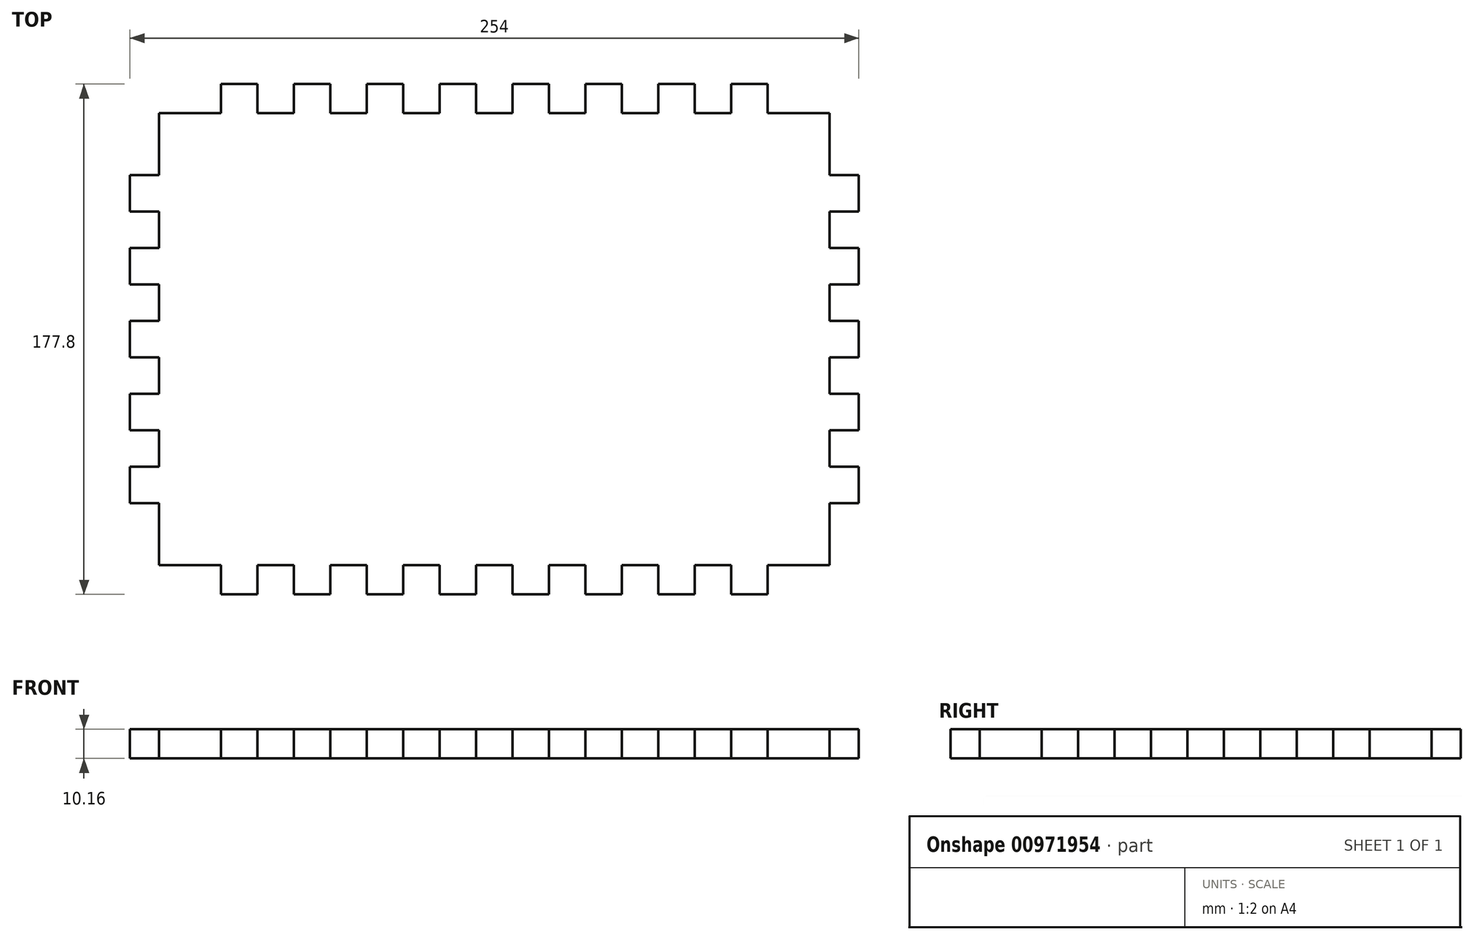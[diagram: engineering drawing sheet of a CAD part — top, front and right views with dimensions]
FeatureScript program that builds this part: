
annotation { "Feature Type Name" : "Feature", "Feature Type Description" : "" }
export const myFeature = defineFeature(function(context is Context, id is Id, definition is map)
    precondition{}
    {
        {
            var Q0;
            Q0=qCreatedBy(makeId("Top.planeOp"),FACE);
            var sketch = newSketch(context, id + "F0", { "sketchPlane" : qUnion([Q0])});
            skLineSegment(sketch, "E0.bottom", {"start": v(31.75, 0) * mm, "end": v(44.45, 0) * mm});
            skLineSegment(sketch, "E1", {"start": v(10.16, -10.16) * mm, "end": v(31.75, -10.16) * mm});
            skLineSegment(sketch, "E2", {"start": v(31.75, -10.16) * mm, "end": v(31.75, 0) * mm});
            skLineSegment(sketch, "E3", {"start": v(44.45, 0) * mm, "end": v(44.45, -10.16) * mm});
            skLineSegment(sketch, "E4", {"start": v(44.45, -10.16) * mm, "end": v(57.15, -10.16) * mm});
            skLineSegment(sketch, "E5", {"start": v(57.15, -10.16) * mm, "end": v(57.15, 0) * mm});
            skLineSegment(sketch, "E6", {"start": v(57.15, 0) * mm, "end": v(69.85, 0) * mm});
            skLineSegment(sketch, "E7", {"start": v(69.85, 0) * mm, "end": v(69.85, -10.16) * mm});
            skLineSegment(sketch, "E8", {"start": v(69.85, -10.16) * mm, "end": v(82.55, -10.16) * mm});
            skLineSegment(sketch, "E9", {"start": v(82.55, -10.16) * mm, "end": v(82.55, 0) * mm});
            skLineSegment(sketch, "E10", {"start": v(82.55, 0) * mm, "end": v(95.25, 0) * mm});
            skLineSegment(sketch, "E11", {"start": v(95.25, 0) * mm, "end": v(95.25, -10.16) * mm});
            skLineSegment(sketch, "E12", {"start": v(95.25, -10.16) * mm, "end": v(107.95, -10.16) * mm});
            skLineSegment(sketch, "E13", {"start": v(107.95, -10.16) * mm, "end": v(107.95, 0) * mm});
            skLineSegment(sketch, "E14", {"start": v(107.95, 0) * mm, "end": v(120.65, 0) * mm});
            skLineSegment(sketch, "E15", {"start": v(120.65, 0) * mm, "end": v(120.65, -10.16) * mm});
            skLineSegment(sketch, "E16", {"start": v(120.65, -10.16) * mm, "end": v(133.35, -10.16) * mm});
            skLineSegment(sketch, "E17", {"start": v(133.35, -10.16) * mm, "end": v(133.35, 0) * mm});
            skPoint(sketch, "E18.orphan", {"position": v(0, 0) * mm});
            skLineSegment(sketch, "E19.trimOffspring", {"start": v(133.35, 0) * mm, "end": v(146.05, 0) * mm});
            skLineSegment(sketch, "E20", {"start": v(146.05, 0) * mm, "end": v(146.05, -10.16) * mm});
            skLineSegment(sketch, "E21", {"start": v(146.05, -10.16) * mm, "end": v(158.75, -10.16) * mm});
            skLineSegment(sketch, "E22", {"start": v(158.75, -10.16) * mm, "end": v(158.75, 0) * mm});
            skLineSegment(sketch, "E23", {"start": v(158.75, 0) * mm, "end": v(171.45, 0) * mm});
            skLineSegment(sketch, "E24", {"start": v(171.45, 0) * mm, "end": v(171.45, -10.16) * mm});
            skLineSegment(sketch, "E25", {"start": v(171.45, -10.16) * mm, "end": v(184.15, -10.16) * mm});
            skLineSegment(sketch, "E26", {"start": v(184.15, -10.16) * mm, "end": v(184.15, 0) * mm});
            skLineSegment(sketch, "E27", {"start": v(184.15, 0) * mm, "end": v(196.85, 0) * mm});
            skLineSegment(sketch, "E28", {"start": v(196.85, 0) * mm, "end": v(196.85, -10.16) * mm});
            skLineSegment(sketch, "E29", {"start": v(196.85, -10.16) * mm, "end": v(209.55, -10.16) * mm});
            skLineSegment(sketch, "E30", {"start": v(209.55, -10.16) * mm, "end": v(209.55, 0) * mm});
            skLineSegment(sketch, "E31.trimOffspring", {"start": v(209.55, 0) * mm, "end": v(222.25, 0) * mm});
            skLineSegment(sketch, "E32", {"start": v(222.25, 0) * mm, "end": v(222.25, -10.16) * mm});
            skLineSegment(sketch, "E33", {"start": v(222.25, -10.16) * mm, "end": v(243.84, -10.16) * mm});
            skPoint(sketch, "E34.orphan", {"position": v(254, 0) * mm});
            skLineSegment(sketch, "E35", {"start": v(10.16, -167.64) * mm, "end": v(31.75, -167.64) * mm});
            skPoint(sketch, "E36.orphan", {"position": v(0, -177.8) * mm});
            skLineSegment(sketch, "E37", {"start": v(127, -10.16) * mm, "end": v(127, -10.16) * mm});
            skLineSegment(sketch, "E38.MirrorCS", {"start": v(222.25, -10.16) * mm, "end": v(222.25, 0) * mm});
            skLineSegment(sketch, "E39.MirrorCS", {"start": v(243.84, -10.16) * mm, "end": v(222.25, -10.16) * mm});
            skLineSegment(sketch, "E40.MirrorCS", {"start": v(243.84, -167.64) * mm, "end": v(222.25, -167.64) * mm});
            skLineSegment(sketch, "E41", {"start": v(10.16, -10.16) * mm, "end": v(10.16, -31.75) * mm});
            skLineSegment(sketch, "E42", {"start": v(10.16, -31.75) * mm, "end": v(0, -31.75) * mm});
            skLineSegment(sketch, "E43", {"start": v(0, -31.75) * mm, "end": v(0, -44.45) * mm});
            skLineSegment(sketch, "E44", {"start": v(0, -44.45) * mm, "end": v(10.16, -44.45) * mm});
            skLineSegment(sketch, "E45", {"start": v(10.16, -44.45) * mm, "end": v(10.16, -57.15) * mm});
            skLineSegment(sketch, "E46", {"start": v(10.16, -57.15) * mm, "end": v(0, -57.15) * mm});
            skLineSegment(sketch, "E47", {"start": v(0, -57.15) * mm, "end": v(0, -69.85) * mm});
            skLineSegment(sketch, "E48", {"start": v(0, -69.85) * mm, "end": v(10.16, -69.85) * mm});
            skLineSegment(sketch, "E49", {"start": v(10.16, -69.85) * mm, "end": v(10.16, -82.55) * mm});
            skLineSegment(sketch, "E50", {"start": v(10.16, -82.55) * mm, "end": v(0, -82.55) * mm});
            skLineSegment(sketch, "E51", {"start": v(0, -82.55) * mm, "end": v(0, -95.25) * mm});
            skLineSegment(sketch, "E52", {"start": v(0, -95.25) * mm, "end": v(10.16, -95.25) * mm});
            skLineSegment(sketch, "E53", {"start": v(10.16, -95.25) * mm, "end": v(10.16, -107.95) * mm});
            skLineSegment(sketch, "E54", {"start": v(10.16, -107.95) * mm, "end": v(0, -107.95) * mm});
            skLineSegment(sketch, "E55", {"start": v(0, -107.95) * mm, "end": v(0, -120.65) * mm});
            skLineSegment(sketch, "E56", {"start": v(0, -120.65) * mm, "end": v(10.16, -120.65) * mm});
            skLineSegment(sketch, "E57", {"start": v(10.16, -120.65) * mm, "end": v(10.16, -133.35) * mm});
            skLineSegment(sketch, "E58", {"start": v(10.16, -133.35) * mm, "end": v(0, -133.35) * mm});
            skLineSegment(sketch, "E59", {"start": v(0, -133.35) * mm, "end": v(0, -146.05) * mm});
            skLineSegment(sketch, "E60", {"start": v(0, -146.05) * mm, "end": v(10.16, -146.05) * mm});
            skLineSegment(sketch, "E61", {"start": v(10.16, -146.05) * mm, "end": v(10.16, -167.64) * mm});
            skLineSegment(sketch, "E62.MirrorCS", {"start": v(243.84, -10.16) * mm, "end": v(243.84, -31.75) * mm});
            skLineSegment(sketch, "E63.MirrorCS", {"start": v(254, -146.05) * mm, "end": v(243.84, -146.05) * mm});
            skLineSegment(sketch, "E64.MirrorCS", {"start": v(254, -44.45) * mm, "end": v(243.84, -44.45) * mm});
            skLineSegment(sketch, "E65.MirrorCS", {"start": v(243.84, -57.15) * mm, "end": v(254, -57.15) * mm});
            skLineSegment(sketch, "E66.MirrorCS", {"start": v(254, -120.65) * mm, "end": v(243.84, -120.65) * mm});
            skLineSegment(sketch, "E67.MirrorCS", {"start": v(243.84, -107.95) * mm, "end": v(254, -107.95) * mm});
            skLineSegment(sketch, "E68.MirrorCS", {"start": v(254, -69.85) * mm, "end": v(243.84, -69.85) * mm});
            skLineSegment(sketch, "E69.MirrorCS", {"start": v(243.84, -82.55) * mm, "end": v(254, -82.55) * mm});
            skLineSegment(sketch, "E70.MirrorCS", {"start": v(254, -95.25) * mm, "end": v(243.84, -95.25) * mm});
            skLineSegment(sketch, "E71.MirrorCS", {"start": v(243.84, -133.35) * mm, "end": v(254, -133.35) * mm});
            skLineSegment(sketch, "E72.MirrorCS", {"start": v(243.84, -31.75) * mm, "end": v(254, -31.75) * mm});
            skLineSegment(sketch, "E73.MirrorCS", {"start": v(254, -31.75) * mm, "end": v(254, -44.45) * mm});
            skLineSegment(sketch, "E74.MirrorCS", {"start": v(254, -107.95) * mm, "end": v(254, -120.65) * mm});
            skLineSegment(sketch, "E75.MirrorCS", {"start": v(254, -57.15) * mm, "end": v(254, -69.85) * mm});
            skLineSegment(sketch, "E76.MirrorCS", {"start": v(243.84, -69.85) * mm, "end": v(243.84, -82.55) * mm});
            skLineSegment(sketch, "E77.MirrorCS", {"start": v(254, -133.35) * mm, "end": v(254, -146.05) * mm});
            skLineSegment(sketch, "E78.MirrorCS", {"start": v(243.84, -95.25) * mm, "end": v(243.84, -107.95) * mm});
            skLineSegment(sketch, "E79.MirrorCS", {"start": v(243.84, -44.45) * mm, "end": v(243.84, -57.15) * mm});
            skLineSegment(sketch, "E80.MirrorCS", {"start": v(254, -82.55) * mm, "end": v(254, -95.25) * mm});
            skLineSegment(sketch, "E81.MirrorCS", {"start": v(243.84, -120.65) * mm, "end": v(243.84, -133.35) * mm});
            skLineSegment(sketch, "E82.MirrorCS", {"start": v(243.84, -146.05) * mm, "end": v(243.84, -167.64) * mm});
            skLineSegment(sketch, "E83", {"start": v(0, -88.9) * mm, "end": v(0, -88.9) * mm});
            skLineSegment(sketch, "E84.MirrorCS", {"start": v(222.25, -167.64) * mm, "end": v(222.25, -177.8) * mm});
            skLineSegment(sketch, "E85.MirrorCS", {"start": v(222.25, -177.8) * mm, "end": v(222.25, -167.64) * mm});
            skLineSegment(sketch, "E86.MirrorCS", {"start": v(31.75, -167.64) * mm, "end": v(31.75, -177.8) * mm});
            skLineSegment(sketch, "E87.MirrorCS", {"start": v(158.75, -167.64) * mm, "end": v(158.75, -177.8) * mm});
            skLineSegment(sketch, "E88.MirrorCS", {"start": v(146.05, -177.8) * mm, "end": v(146.05, -167.64) * mm});
            skLineSegment(sketch, "E89.MirrorCS", {"start": v(69.85, -177.8) * mm, "end": v(69.85, -167.64) * mm});
            skLineSegment(sketch, "E90.MirrorCS", {"start": v(95.25, -177.8) * mm, "end": v(95.25, -167.64) * mm});
            skLineSegment(sketch, "E91.MirrorCS", {"start": v(107.95, -167.64) * mm, "end": v(107.95, -177.8) * mm});
            skLineSegment(sketch, "E92.MirrorCS", {"start": v(120.65, -167.64) * mm, "end": v(133.35, -167.64) * mm});
            skLineSegment(sketch, "E93.MirrorCS", {"start": v(171.45, -177.8) * mm, "end": v(171.45, -167.64) * mm});
            skLineSegment(sketch, "E94.MirrorCS", {"start": v(196.85, -177.8) * mm, "end": v(196.85, -167.64) * mm});
            skLineSegment(sketch, "E95.MirrorCS", {"start": v(184.15, -167.64) * mm, "end": v(184.15, -177.8) * mm});
            skLineSegment(sketch, "E96.MirrorCS", {"start": v(57.15, -167.64) * mm, "end": v(57.15, -177.8) * mm});
            skLineSegment(sketch, "E97.MirrorCS", {"start": v(133.35, -167.64) * mm, "end": v(133.35, -177.8) * mm});
            skLineSegment(sketch, "E98.MirrorCS", {"start": v(44.45, -177.8) * mm, "end": v(44.45, -167.64) * mm});
            skLineSegment(sketch, "E99.MirrorCS", {"start": v(82.55, -167.64) * mm, "end": v(82.55, -177.8) * mm});
            skLineSegment(sketch, "E100.MirrorCS", {"start": v(209.55, -167.64) * mm, "end": v(209.55, -177.8) * mm});
            skLineSegment(sketch, "E101.MirrorCS", {"start": v(120.65, -177.8) * mm, "end": v(120.65, -167.64) * mm});
            skLineSegment(sketch, "E102.MirrorCS", {"start": v(184.15, -177.8) * mm, "end": v(196.85, -177.8) * mm});
            skLineSegment(sketch, "E103.MirrorCS", {"start": v(82.55, -177.8) * mm, "end": v(95.25, -177.8) * mm});
            skLineSegment(sketch, "E104.MirrorCS", {"start": v(209.55, -177.8) * mm, "end": v(222.25, -177.8) * mm});
            skLineSegment(sketch, "E105.MirrorCS", {"start": v(133.35, -177.8) * mm, "end": v(146.05, -177.8) * mm});
            skLineSegment(sketch, "E106.MirrorCS", {"start": v(57.15, -177.8) * mm, "end": v(69.85, -177.8) * mm});
            skLineSegment(sketch, "E107.MirrorCS", {"start": v(31.75, -177.8) * mm, "end": v(44.45, -177.8) * mm});
            skLineSegment(sketch, "E108.MirrorCS", {"start": v(158.75, -177.8) * mm, "end": v(171.45, -177.8) * mm});
            skLineSegment(sketch, "E109.MirrorCS", {"start": v(107.95, -177.8) * mm, "end": v(120.65, -177.8) * mm});
            skLineSegment(sketch, "E110.MirrorCS", {"start": v(146.05, -167.64) * mm, "end": v(158.75, -167.64) * mm});
            skLineSegment(sketch, "E111.MirrorCS", {"start": v(95.25, -167.64) * mm, "end": v(107.95, -167.64) * mm});
            skLineSegment(sketch, "E112.MirrorCS", {"start": v(127, -167.64) * mm, "end": v(127, -167.64) * mm});
            skLineSegment(sketch, "E113.MirrorCS", {"start": v(44.45, -167.64) * mm, "end": v(57.15, -167.64) * mm});
            skLineSegment(sketch, "E114.MirrorCS", {"start": v(69.85, -167.64) * mm, "end": v(82.55, -167.64) * mm});
            skLineSegment(sketch, "E115.MirrorCS", {"start": v(196.85, -167.64) * mm, "end": v(209.55, -167.64) * mm});
            skLineSegment(sketch, "E116.MirrorCS", {"start": v(171.45, -167.64) * mm, "end": v(184.15, -167.64) * mm});
            skSolve(sketch);
        }
        {
            var Q0;
            Q0=makeQuery(id+"F0.imprint","IMPRINT",FACE,{"disambiguationData":[TD([[makeQuery(id+"F0.imprint","IMPRINT",EDGE,{"derivedFrom":sQuery(id+"F0.wireOp",EDGE,"E1")}),-1.0]])]});
            extrude(context, id + "F1", {"entities" : qUnion([Q0]), "depth" : 10.16 * mm, "offsetDistance" : 25.4 * mm});
        }
    });
